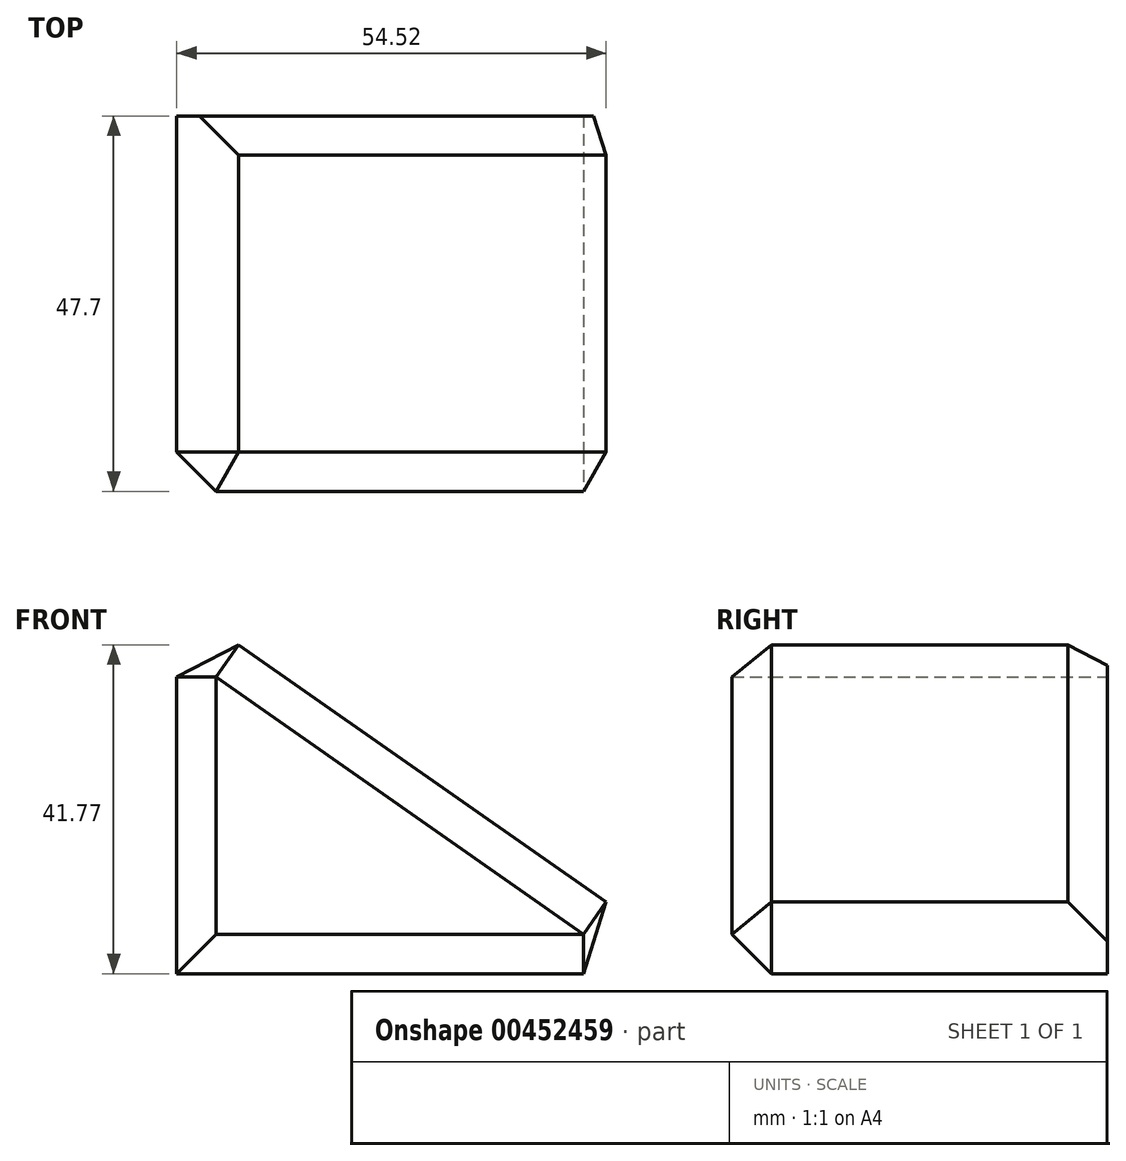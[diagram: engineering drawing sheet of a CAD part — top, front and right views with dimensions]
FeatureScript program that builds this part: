
annotation { "Feature Type Name" : "Feature", "Feature Type Description" : "" }
export const myFeature = defineFeature(function(context is Context, id is Id, definition is map)
    precondition{}
    {
        {
            var Q0;
            Q0=qCreatedBy(makeId("Front.planeOp"),FACE);
            var sketch = newSketch(context, id + "F0", { "sketchPlane" : qUnion([Q0])});
            skLineSegment(sketch, "E0", {"start": v(0, 0) * mm, "end": v(-67.5, 0) * mm});
            skLineSegment(sketch, "E1", {"start": v(-67.5, 0) * mm, "end": v(-67.5, 47.29) * mm});
            skLineSegment(sketch, "E2", {"start": v(-67.5, 47.29) * mm, "end": v(0, 0) * mm});
            skSolve(sketch);
        }
        {
            var Q0;
            Q0=makeQuery(id+"F0.imprint","IMPRINT",FACE,{"disambiguationData":[TD([[makeQuery(id+"F0.imprint","IMPRINT",EDGE,{"derivedFrom":sQuery(id+"F0.wireOp",EDGE,"E0")}),-1.0]])]});
            extrude(context, id + "F1", {"entities" : qUnion([Q0]), "depth" : 47.7 * mm});
        }
        {
            var Q0;
            Q0=makeQuery(id+"F1.opExtrude","CAP_FACE",FACE,{"disambiguationData":[OSD([sQuery(id+"F0.wireOp",EDGE,"E0"),sQuery(id+"F0.wireOp",EDGE,"E1"),sQuery(id+"F0.wireOp",EDGE,"E2")])],"isStart":false});
            var Q1;
            Q1=makeQuery(id+"F1.opExtrude","SWEPT_FACE",FACE,{"disambiguationData":[OSD([sQuery(id+"F0.wireOp",EDGE,"E2")])]});
            chamfer(context, id + "F2", {"entities" : qUnion([Q0, Q1]), "width" : 5 * mm, "tangentPropagation" : true});
        }
    });
